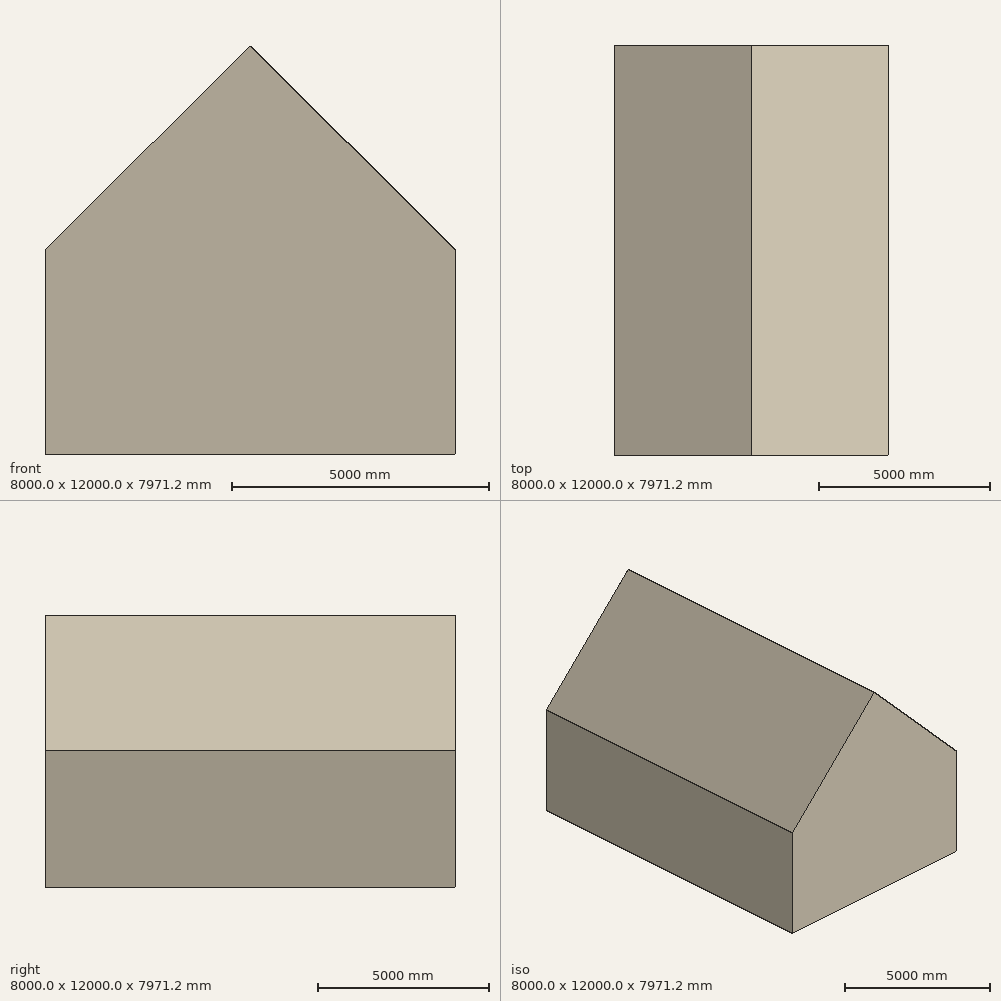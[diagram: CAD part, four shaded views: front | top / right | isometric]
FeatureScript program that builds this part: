
annotation { "Feature Type Name" : "Feature", "Feature Type Description" : "" }
export const myFeature = defineFeature(function(context is Context, id is Id, definition is map)
    precondition{}
    {
        {
            var Q0;
            Q0=qCreatedBy(makeId("Front.planeOp"),FACE);
            var sketch = newSketch(context, id + "F0", { "sketchPlane" : qUnion([Q0])});
            skLineSegment(sketch, "E0", {"start": v(0, 0) * mm, "end": v(4000, 0) * mm});
            skLineSegment(sketch, "E1", {"start": v(4000, 0) * mm, "end": v(4000, 4000) * mm});
            skLineSegment(sketch, "E2", {"start": v(4000, 4000) * mm, "end": v(0, 7971.2) * mm});
            skLineSegment(sketch, "E3", {"start": v(0, 0) * mm, "end": v(-4000, 0) * mm});
            skLineSegment(sketch, "E4", {"start": v(-4000, 0) * mm, "end": v(-4000, 4000) * mm});
            skLineSegment(sketch, "E5", {"start": v(-4000, 4000) * mm, "end": v(0, 7971.2) * mm});
            skLineSegment(sketch, "E6", {"start": v(0, 2189.08) * mm, "end": v(0, 1494.09) * mm});
            skSolve(sketch);
        }
        {
            var Q0;
            Q0=makeQuery(id+"F0.imprint","IMPRINT",FACE,{"disambiguationData":[TD([[makeQuery(id+"F0.imprint","IMPRINT",EDGE,{"derivedFrom":sQuery(id+"F0.wireOp",EDGE,"E0")}),1.0]])]});
            extrude(context, id + "F1", {"entities" : qUnion([Q0]), "depth" : 12000 * mm});
        }
    });
